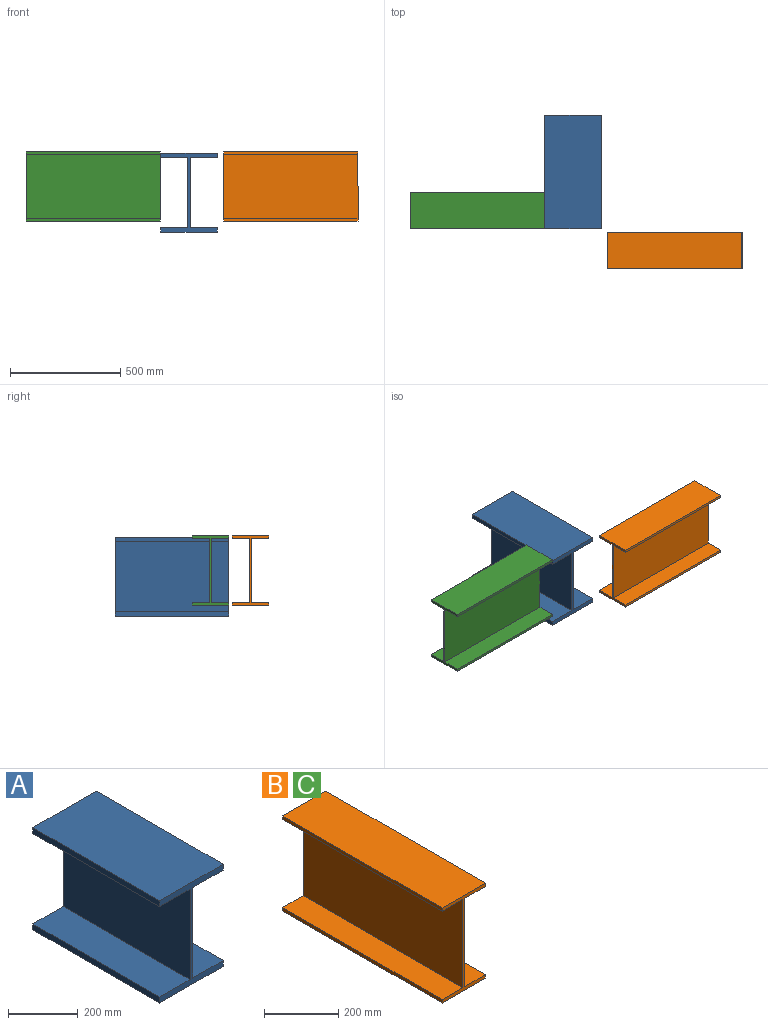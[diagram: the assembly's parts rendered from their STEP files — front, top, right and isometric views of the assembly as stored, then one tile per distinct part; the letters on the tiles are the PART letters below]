
ASSEMBLY  parts=3 mates=4
PART A: 14 faces, bbox 257.2x514.1x358.8 mm
  f0: plane 514.1x257.18mm, normal (0,0,-1), area 132212.6mm2, adj f1,f11,f12,f13
  f1: plane 514.1x20.64mm, normal (1,0,0), area 10609.7mm2, adj f0,f2,f12,f13
  f2: plane 514.1x123.03mm, normal (0,0,1), area 63249.9mm2, adj f1,f3,f12,f13
  f3: plane 514.1x317.5mm, normal (1,0,0), area 163225.5mm2, adj f2,f4,f12,f13
  f4: plane 514.1x123.03mm, normal (0,0,-1), area 63249.9mm2, adj f3,f5,f12,f13
  f5: plane 514.1x20.64mm, normal (1,0,0), area 10609.7mm2, adj f4,f6,f12,f13
  f6: plane 514.1x257.18mm, normal (0,0,1), area 132212.6mm2, adj f5,f7,f12,f13
  f7: plane 514.1x20.64mm, normal (-1,0,0), area 10609.7mm2, adj f6,f8,f12,f13
  f8: plane 514.1x123.03mm, normal (0,0,-1), area 63249.9mm2, adj f7,f9,f12,f13
  f9: plane 514.1x317.5mm, normal (-1,0,0), area 163225.5mm2, adj f8,f10,f12,f13
  f10: plane 514.1x123.03mm, normal (0,0,1), area 63249.9mm2, adj f9,f11,f12,f13
  f11: plane 514.1x20.64mm, normal (-1,0,0), area 10609.7mm2, adj f0,f10,f12,f13
  f12: plane 358.78x257.18mm, normal (0,-1,0), area 14143.1mm2, adj f0,f1,f2,f3,f4,f5,f6,f7
  f13: plane 358.78x257.18mm, normal (0,1,0), area 14143.1mm2, adj f0,f1,f2,f3,f4,f5,f6,f7
PART B: 14 faces, bbox 165.1x609.6x314.3 mm
  f0: plane 609.6x165.1mm, normal (0,0,-1), area 100645mm2, adj f1,f11,f12,f13
  f1: plane 609.6x11.11mm, normal (1,0,0), area 6774.2mm2, adj f0,f2,f12,f13
  f2: plane 609.6x79.38mm, normal (0,0,1), area 48387mm2, adj f1,f3,f12,f13
  f3: plane 609.6x292.1mm, normal (1,0,0), area 178064.2mm2, adj f2,f4,f12,f13
  f4: plane 609.6x79.38mm, normal (0,0,-1), area 48387mm2, adj f3,f5,f12,f13
  f5: plane 609.6x11.11mm, normal (1,0,0), area 6774.2mm2, adj f4,f6,f12,f13
  f6: plane 609.6x165.1mm, normal (0,0,1), area 100645mm2, adj f5,f7,f12,f13
  f7: plane 609.6x11.11mm, normal (-1,0,0), area 6774.2mm2, adj f6,f8,f12,f13
  f8: plane 609.6x79.38mm, normal (0,0,-1), area 48387mm2, adj f7,f9,f12,f13
  f9: plane 609.6x292.1mm, normal (-1,0,0), area 178064.2mm2, adj f8,f10,f12,f13
  f10: plane 609.6x79.38mm, normal (0,0,1), area 48387mm2, adj f9,f11,f12,f13
  f11: plane 609.6x11.11mm, normal (-1,0,0), area 6774.2mm2, adj f0,f10,f12,f13
  f12: plane 314.33x165.1mm, normal (0,-1,0), area 5524.2mm2, adj f0,f1,f2,f3,f4,f5,f6,f7
  f13: plane 314.33x165.1mm, normal (0,1,0), area 5524.2mm2, adj f0,f1,f2,f3,f4,f5,f6,f7
PART C: same geometry as B
PLACE A t=(34.73,239.07,53.27)mm fixed
PLACE B rot(axis=(-0.71,-0.71,0),180deg) t=(800.81,-374.64,81.26)mm
PLACE C rot(axis=(-0.71,0.71,0),180deg) t=(-704.52,-192.47,81.26)mm
MATE parallel A.f12 <-> C.f3  axis (0,-1,0) through (40.29,-275.02,212.02)mm
MATE parallel C.f12 <-> B.f12  axis (1,0,0) through (-94.92,-192.47,81.26)mm
MATE planar C.f1 <-> A.f12  axis (0,-1,0) through (-399.72,-275.02,232.87)mm
MATE planar B.f6 <-> C.f6  axis (0,0,-1) through (496.01,-374.64,-75.9)mm
